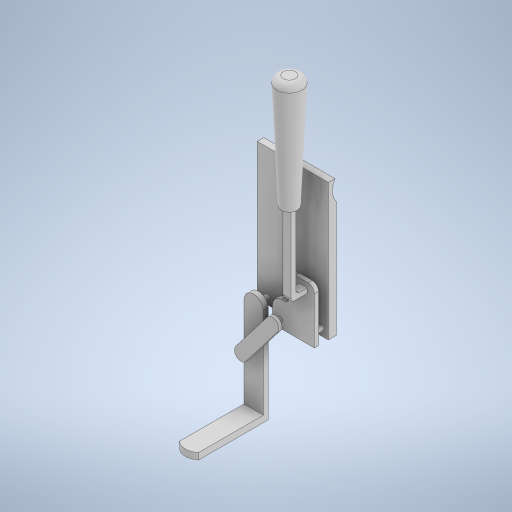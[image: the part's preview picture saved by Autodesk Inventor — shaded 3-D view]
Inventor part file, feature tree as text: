
AUTODESK INVENTOR PART (.ipt)
format: ipt  version: 2023 (Build 270158000, 158)  size: 454,144 bytes
history: native  units: in
note: dims shown in document units (in); Inventor stores cm internally (conversion verified against a paired STEP export)
features: sketch x18, extrude x16, fillet x3, draft x1, direct_edit x1, mirror x1, other x1
ambient origin geometry x8: Origin, YZ Plane, XZ Plane, XY Plane, X Axis, Y Axis, Z Axis, Center Point
bodies: Solid1 (feature_tree)
feature tree (41):
  extrude  "Extrusion1"  Depth=1.6624in
  extrude  "Extrusion2"  Depth=0.875in
  extrude  "Extrusion3"  Depth=0.0591in
  extrude  "Extrusion4"  Depth=0.315in
  sketch  "Sketch5"  dims[d11=0.315in d12=0.6496in]
  extrude  "Extrusion5"  Depth=0.6496in
  extrude  "Extrusion6"  Depth=0.0787in
  extrude  "Extrusion7"  Depth=0.0394in
  extrude  "Extrusion8"  Depth=0.1181in TaperAngle=0.0deg
  sketch  "Sketch10"  dims[d25=1.1811in d26=0.0591in d27=0.0in d28=0.0591in]
  extrude  "Extrusion9"  Depth=0.1181in TaperAngle=0.0deg
  fillet  "Fillet1"  Radius=0.1181in
  fillet  "Fillet2"  Radius=0.1181in
  extrude  "Extrusion10"  Depth=0.0591in TaperAngle=0.0deg
  draft  "FaceDraft1"
  fillet  "Fillet3"  Radius=0.0591in
  extrude  "Extrusion11"  Depth=0.1181in
  extrude  "Extrusion12"  Depth=0.0591in
  extrude  "Extrusion13"  Depth=0.1969in TaperAngle=0.0deg
  extrude  "Extrusion14"  Depth=0.0591in TaperAngle=0.0deg
  extrude  "Extrusion15"  Depth=0.0394in
  extrude  "Extrusion16"  Depth=0.315in
  direct_edit  "Direct Edit1"
  mirror  "Mirror1"
  sketch  "Sketch1"  dims[d0=0.8661in d1=1.6624in]
  sketch  "Sketch2"  dims[d2=0.0984in d3=0.0in d4=0.875in]
  sketch  "Sketch3"  dims[d5=0.0in d6=0.0in d7=0.0591in]
  sketch  "Sketch4"  dims[d8=0.1181in d9=0.0in d10=0.315in]
  sketch  "Sketch6"  dims[d13=0.5118in d14=0.0787in]
  sketch  "Sketch7"  dims[d15=0.0787in d16=0.0394in]
  sketch  "Sketch8"  dims[d17=0.1181in d18=0.0512in d19=0.0in]
  sketch  "Sketch9"  dims[d20=0.0591in d21=0.1181in d22=0.0in d23=0.1181in d24=0.1181in]
  sketch  "Sketch11"  dims[d29=0.1181in d30=0.0in d31=0.0984in]
  sketch  "Sketch12"  dims[d32=0.0591in d33=0.0591in]
  sketch  "Sketch13"  dims[d34=0.0886in d35=0.1969in d36=0.0in]
  sketch  "Sketch14"  dims[d37=0.0591in d38=0.9252in d39=0.0in]
  sketch  "Sketch15"  dims[d40=0.0394in d41=0.0394in]
  sketch  "Sketch16"  dims[d42=0.0295in d43=0.315in]
  sketch  "Sketch17"  dims[d44=1.378in d45=0.0in]
  sketch  "Sketch18"  dims[d46=0.0172in d47=0.0787in d48=0.5118in d49=0.0591in d50=0.1181in d51=0.0in d52=0.1575in d54=0.0394in d55=0.0in d56=0.0787in d57=0.7874in d58=0.0in d59=0.1737in d60=0.0787in d61=0.0in d62=0.3937in d63=0.0in d64=0.4375in d65=0.0in d66=0.0in d67=0.7874in d68=0.3937in d69=0.3937in]
  other  "Scale1"
